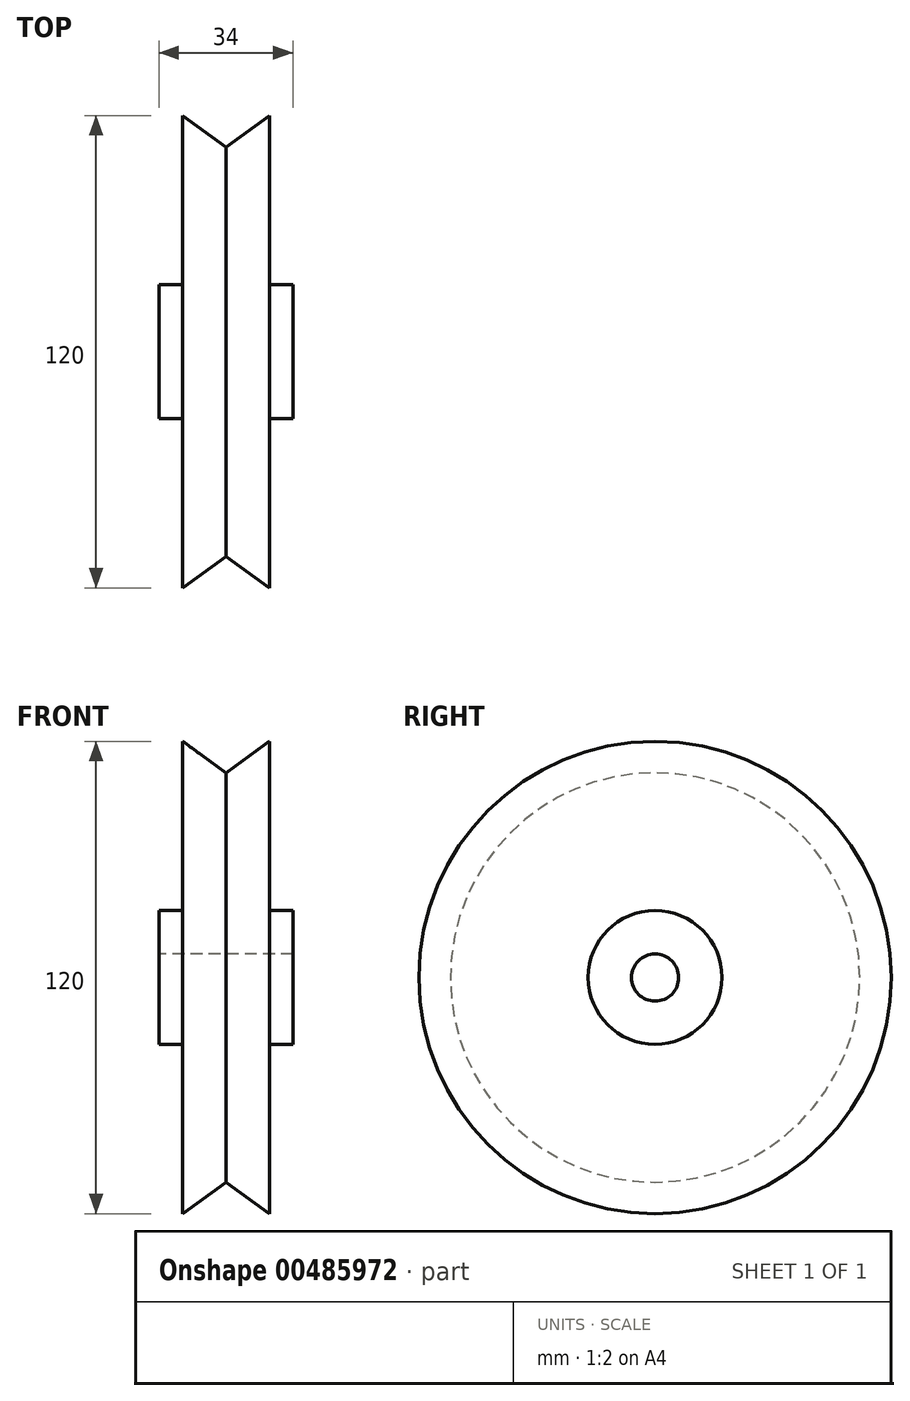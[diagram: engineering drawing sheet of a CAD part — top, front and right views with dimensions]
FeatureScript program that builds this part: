
annotation { "Feature Type Name" : "Feature", "Feature Type Description" : "" }
export const myFeature = defineFeature(function(context is Context, id is Id, definition is map)
    precondition{}
    {
        {
            var Q0;
            Q0=qCreatedBy(makeId("Top.planeOp"),FACE);
            var sketch = newSketch(context, id + "F0", { "sketchPlane" : qUnion([Q0])});
            skLineSegment(sketch, "E0", {"start": v(0, 47.97) * mm, "end": v(0, -45.27) * mm, "construction": true});
            skLineSegment(sketch, "E1", {"start": v(-40.81, 0) * mm, "end": v(48.24, 0) * mm, "construction": true});
            skLineSegment(sketch, "E2", {"start": v(-17, 6) * mm, "end": v(0, 6) * mm});
            skLineSegment(sketch, "E3", {"start": v(-17, 6) * mm, "end": v(-17, 17) * mm});
            skLineSegment(sketch, "E4", {"start": v(-17, 17) * mm, "end": v(-11, 17) * mm});
            skLineSegment(sketch, "E5", {"start": v(-11, 17) * mm, "end": v(-11, 60) * mm});
            skLineSegment(sketch, "E6", {"start": v(-11, 60) * mm, "end": v(0, 52) * mm});
            skLineSegment(sketch, "E7.MirrorCS", {"start": v(11, 60) * mm, "end": v(0, 52) * mm});
            skLineSegment(sketch, "E8.MirrorCS", {"start": v(11, 17) * mm, "end": v(11, 60) * mm});
            skLineSegment(sketch, "E9.MirrorCS", {"start": v(17, 6) * mm, "end": v(0, 6) * mm});
            skLineSegment(sketch, "E10.MirrorCS", {"start": v(17, 6) * mm, "end": v(17, 17) * mm});
            skLineSegment(sketch, "E11.MirrorCS", {"start": v(17, 17) * mm, "end": v(11, 17) * mm});
            skSolve(sketch);
        }
        {
            var Q0;
            Q0=makeQuery(id+"F0.imprint","IMPRINT",FACE,{"disambiguationData":[TD([[makeQuery(id+"F0.imprint","IMPRINT",EDGE,{"derivedFrom":sQuery(id+"F0.wireOp",EDGE,"E2")}),1.0]])]});
            var Q1;
            Q1=sQuery(id+"F0.wireOp",EDGE,"E1");
            revolve(context, id + "F1", {"entities" : qUnion([Q0]), "axis" : qUnion([Q1]), "revolveType" : RevolveType.FULL});
        }
    });
